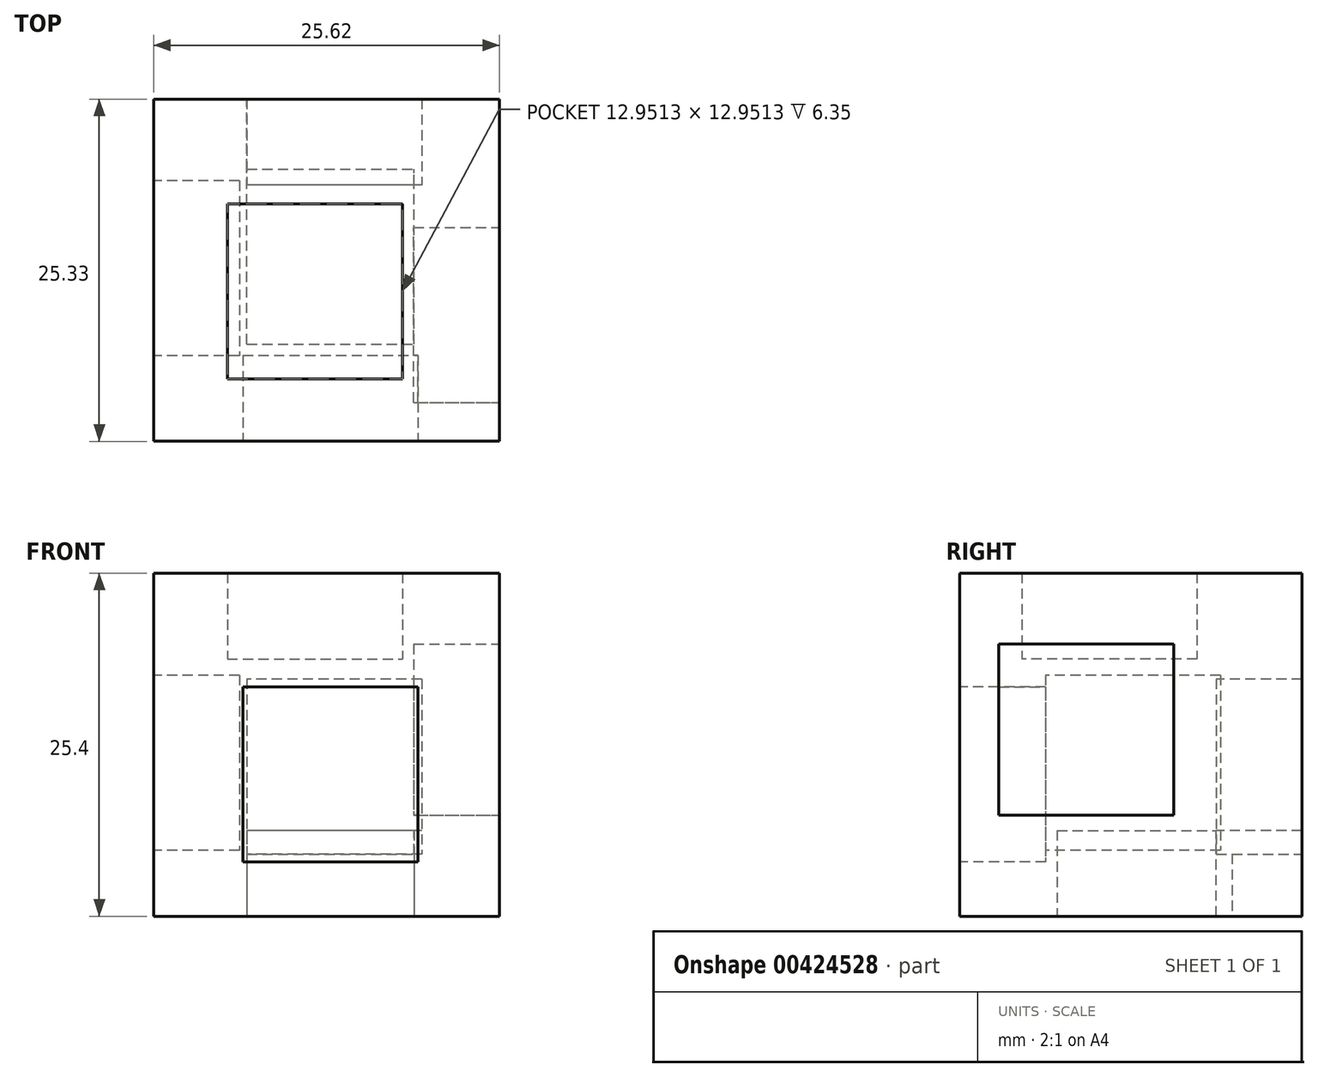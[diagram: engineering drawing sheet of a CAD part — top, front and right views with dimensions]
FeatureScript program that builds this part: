
annotation { "Feature Type Name" : "Feature", "Feature Type Description" : "" }
export const myFeature = defineFeature(function(context is Context, id is Id, definition is map)
    precondition{}
    {
        {
            var Q0;
            Q0=qCreatedBy(makeId("Top.planeOp"),FACE);
            var sketch = newSketch(context, id + "F0", { "sketchPlane" : qUnion([Q0])});
            skLineSegment(sketch, "E0.bottom", {"start": v(-29.36, 32.52) * mm, "end": v(-3.74, 32.52) * mm});
            skLineSegment(sketch, "E0.top", {"start": v(-29.36, 7.2) * mm, "end": v(-3.74, 7.2) * mm});
            skLineSegment(sketch, "E0.left", {"start": v(-29.36, 32.52) * mm, "end": v(-29.36, 7.2) * mm});
            skLineSegment(sketch, "E0.right", {"start": v(-3.74, 32.52) * mm, "end": v(-3.74, 7.2) * mm});
            skSolve(sketch);
        }
        {
            var Q0;
            Q0=makeQuery(id+"F0.imprint","IMPRINT",FACE,{"disambiguationData":[TD([[makeQuery(id+"F0.imprint","IMPRINT",EDGE,{"derivedFrom":sQuery(id+"F0.wireOp",EDGE,"E0.bottom")}),-1.0]])]});
            extrude(context, id + "F1", {"entities" : qUnion([Q0]), "depth" : 25.4 * mm});
        }
        {
            var Q0;
            Q0=makeQuery(id+"F1.opExtrude","SWEPT_FACE",FACE,{"disambiguationData":[OSD([sQuery(id+"F0.wireOp",EDGE,"E0.right")])]});
            var sketch = newSketch(context, id + "F2", { "sketchPlane" : qUnion([Q0])});
            skLineSegment(sketch, "E1.bottom", {"start": v(10.07, 20.15) * mm, "end": v(23.02, 20.15) * mm});
            skLineSegment(sketch, "E1.top", {"start": v(10.07, 7.48) * mm, "end": v(23.02, 7.48) * mm});
            skLineSegment(sketch, "E1.left", {"start": v(10.07, 20.15) * mm, "end": v(10.07, 7.48) * mm});
            skLineSegment(sketch, "E1.right", {"start": v(23.02, 20.15) * mm, "end": v(23.02, 7.48) * mm});
            skSolve(sketch);
        }
        {
            var Q0;
            Q0=makeQuery(id+"F2.imprint","IMPRINT",FACE,{"disambiguationData":[TD([[makeQuery(id+"F2.imprint","IMPRINT",EDGE,{"derivedFrom":sQuery(id+"F2.wireOp",EDGE,"E1.bottom")}),-1.0]])]});
            extrude(context, id + "F3", {"entities" : qUnion([Q0]), "operationType" : NewBodyOperationType.REMOVE, "oppositeDirection" : true, "depth" : 6.35 * mm});
        }
        {
            var Q0;
            Q0=makeQuery(id+"F1.opExtrude","SWEPT_FACE",FACE,{"disambiguationData":[OSD([sQuery(id+"F0.wireOp",EDGE,"E0.left")])]});
            var sketch = newSketch(context, id + "F4", { "sketchPlane" : qUnion([Q0])});
            skLineSegment(sketch, "E2.bottom", {"start": v(-26.48, 17.84) * mm, "end": v(-13.53, 17.84) * mm});
            skLineSegment(sketch, "E2.top", {"start": v(-26.48, 4.9) * mm, "end": v(-13.53, 4.9) * mm});
            skLineSegment(sketch, "E2.left", {"start": v(-26.48, 17.84) * mm, "end": v(-26.48, 4.9) * mm});
            skLineSegment(sketch, "E2.right", {"start": v(-13.53, 17.84) * mm, "end": v(-13.53, 4.9) * mm});
            skSolve(sketch);
        }
        {
            var Q0;
            Q0 = qSketchRegion(id + "F4", true);
            extrude(context, id + "F5", {"entities" : qUnion([Q0]), "operationType" : NewBodyOperationType.REMOVE, "oppositeDirection" : true, "depth" : 6.35 * mm});
        }
        {
            var Q0;
            Q0=makeQuery(id+"F1.opExtrude","CAP_FACE",FACE,{"disambiguationData":[OSD([sQuery(id+"F0.wireOp",EDGE,"E0.bottom"),sQuery(id+"F0.wireOp",EDGE,"E0.top"),sQuery(id+"F0.wireOp",EDGE,"E0.left"),sQuery(id+"F0.wireOp",EDGE,"E0.right")])],"isStart":false});
            var sketch = newSketch(context, id + "F6", { "sketchPlane" : qUnion([Q0])});
            skLineSegment(sketch, "E3.bottom", {"start": v(-23.89, 24.75) * mm, "end": v(-10.94, 24.75) * mm});
            skLineSegment(sketch, "E3.top", {"start": v(-23.89, 11.8) * mm, "end": v(-10.94, 11.8) * mm});
            skLineSegment(sketch, "E3.left", {"start": v(-23.89, 24.75) * mm, "end": v(-23.89, 11.8) * mm});
            skLineSegment(sketch, "E3.right", {"start": v(-10.94, 24.75) * mm, "end": v(-10.94, 11.8) * mm});
            skSolve(sketch);
        }
        {
            var Q0;
            Q0 = qSketchRegion(id + "F6", true);
            extrude(context, id + "F7", {"entities" : qUnion([Q0]), "operationType" : NewBodyOperationType.REMOVE, "oppositeDirection" : true, "depth" : 6.35 * mm});
        }
        {
            var Q0;
            Q0=makeQuery(id+"F1.opExtrude","SWEPT_FACE",FACE,{"disambiguationData":[OSD([sQuery(id+"F0.wireOp",EDGE,"E0.bottom")])]});
            var sketch = newSketch(context, id + "F8", { "sketchPlane" : qUnion([Q0])});
            skLineSegment(sketch, "E4.bottom", {"start": v(9.5, 17.56) * mm, "end": v(22.45, 17.56) * mm});
            skLineSegment(sketch, "E4.top", {"start": v(9.5, 4.6) * mm, "end": v(22.45, 4.6) * mm});
            skLineSegment(sketch, "E4.left", {"start": v(9.5, 17.56) * mm, "end": v(9.5, 4.6) * mm});
            skLineSegment(sketch, "E4.right", {"start": v(22.45, 17.56) * mm, "end": v(22.45, 4.6) * mm});
            skSolve(sketch);
        }
        {
            var Q0;
            Q0 = qSketchRegion(id + "F8", true);
            extrude(context, id + "F9", {"entities" : qUnion([Q0]), "operationType" : NewBodyOperationType.REMOVE, "oppositeDirection" : true, "depth" : 6.35 * mm});
        }
        {
            var Q0;
            Q0=makeQuery(id+"F1.opExtrude","SWEPT_FACE",FACE,{"disambiguationData":[OSD([sQuery(id+"F0.wireOp",EDGE,"E0.top")])]});
            var sketch = newSketch(context, id + "F10", { "sketchPlane" : qUnion([Q0])});
            skLineSegment(sketch, "E5.bottom", {"start": v(-22.74, 16.98) * mm, "end": v(-9.79, 16.98) * mm});
            skLineSegment(sketch, "E5.top", {"start": v(-22.74, 4.03) * mm, "end": v(-9.79, 4.03) * mm});
            skLineSegment(sketch, "E5.left", {"start": v(-22.74, 16.98) * mm, "end": v(-22.74, 4.03) * mm});
            skLineSegment(sketch, "E5.right", {"start": v(-9.79, 16.98) * mm, "end": v(-9.79, 4.03) * mm});
            skSolve(sketch);
        }
        {
            var Q0;
            Q0=makeQuery(id+"F10.imprint","IMPRINT",FACE,{"disambiguationData":[TD([[makeQuery(id+"F10.imprint","IMPRINT",EDGE,{"derivedFrom":sQuery(id+"F10.wireOp",EDGE,"E5.bottom")}),-1.0]])]});
            extrude(context, id + "F11", {"entities" : qUnion([Q0]), "operationType" : NewBodyOperationType.REMOVE, "oppositeDirection" : true, "depth" : 6.35 * mm});
        }
        {
            var Q0;
            Q0=makeQuery(id+"F1.opExtrude","CAP_FACE",FACE,{"disambiguationData":[OSD([sQuery(id+"F0.wireOp",EDGE,"E0.bottom"),sQuery(id+"F0.wireOp",EDGE,"E0.top"),sQuery(id+"F0.wireOp",EDGE,"E0.left"),sQuery(id+"F0.wireOp",EDGE,"E0.right")])],"isStart":true});
            var sketch = newSketch(context, id + "F12", { "sketchPlane" : qUnion([Q0])});
            skLineSegment(sketch, "E6.bottom", {"start": v(-22.45, -14.4) * mm, "end": v(-10.07, -14.4) * mm});
            skLineSegment(sketch, "E6.top", {"start": v(-22.45, -27.34) * mm, "end": v(-10.07, -27.34) * mm});
            skLineSegment(sketch, "E6.left", {"start": v(-22.45, -14.4) * mm, "end": v(-22.45, -27.34) * mm});
            skLineSegment(sketch, "E6.right", {"start": v(-10.07, -14.4) * mm, "end": v(-10.07, -27.34) * mm});
            skSolve(sketch);
        }
        {
            var Q0;
            Q0 = qSketchRegion(id + "F12", true);
            extrude(context, id + "F13", {"entities" : qUnion([Q0]), "operationType" : NewBodyOperationType.REMOVE, "oppositeDirection" : true, "depth" : 6.35 * mm});
        }
        {
            var Q0;
            Q0=makeQuery(id+"F7.boolean.opBoolean","COPY",FACE,{"derivedFrom":makeQuery(id+"F7.opExtrude","CAP_FACE",FACE,{"disambiguationData":[OSD([sQuery(id+"F6.wireOp",EDGE,"E3.bottom"),sQuery(id+"F6.wireOp",EDGE,"E3.top"),sQuery(id+"F6.wireOp",EDGE,"E3.left"),sQuery(id+"F6.wireOp",EDGE,"E3.right")])],"isStart":false})});
            var sketch = newSketch(context, id + "F14", { "sketchPlane" : qUnion([Q0])});
            skLineSegment(sketch, "E7.bottom", {"start": v(-23.89, 24.75) * mm, "end": v(-10.94, 24.75) * mm});
            skLineSegment(sketch, "E7.top", {"start": v(-23.89, 11.8) * mm, "end": v(-10.94, 11.8) * mm});
            skLineSegment(sketch, "E7.left", {"start": v(-23.89, 24.75) * mm, "end": v(-23.89, 11.8) * mm});
            skLineSegment(sketch, "E7.right", {"start": v(-10.94, 24.75) * mm, "end": v(-10.94, 11.8) * mm});
            skSolve(sketch);
        }
        {
            var Q0;
            Q0 = qSketchRegion(id + "F14", true);
            extrude(context, id + "F15", {"entities" : qUnion([Q0]), "depth" : 6.35 * mm});
        }
        {
            var Q0;
            Q0=makeQuery(id+"F9.boolean.opBoolean","COPY",FACE,{"derivedFrom":makeQuery(id+"F9.opExtrude","CAP_FACE",FACE,{"disambiguationData":[OSD([sQuery(id+"F8.wireOp",EDGE,"E4.bottom"),sQuery(id+"F8.wireOp",EDGE,"E4.top"),sQuery(id+"F8.wireOp",EDGE,"E4.left"),sQuery(id+"F8.wireOp",EDGE,"E4.right")])],"isStart":false})});
            var sketch = newSketch(context, id + "F16", { "sketchPlane" : qUnion([Q0])});
            skLineSegment(sketch, "E8.bottom", {"start": v(9.5, 17.56) * mm, "end": v(22.45, 17.56) * mm});
            skLineSegment(sketch, "E8.top", {"start": v(9.5, 6.35) * mm, "end": v(22.45, 6.35) * mm});
            skLineSegment(sketch, "E8.left", {"start": v(9.5, 17.56) * mm, "end": v(9.5, 6.35) * mm});
            skLineSegment(sketch, "E8.right", {"start": v(22.45, 17.56) * mm, "end": v(22.45, 6.35) * mm});
            skSolve(sketch);
        }
        {
            var Q0;
            Q0 = qSketchRegion(id + "F16", true);
            extrude(context, id + "F17", {"entities" : qUnion([Q0]), "depth" : 6.35 * mm});
        }
        {
            var Q0;
            Q0=makeQuery(id+"F5.boolean.opBoolean","COPY",FACE,{"derivedFrom":makeQuery(id+"F5.opExtrude","CAP_FACE",FACE,{"disambiguationData":[OSD([sQuery(id+"F4.wireOp",EDGE,"E2.bottom"),sQuery(id+"F4.wireOp",EDGE,"E2.top"),sQuery(id+"F4.wireOp",EDGE,"E2.left"),sQuery(id+"F4.wireOp",EDGE,"E2.right")])],"isStart":false})});
            var sketch = newSketch(context, id + "F18", { "sketchPlane" : qUnion([Q0])});
            skLineSegment(sketch, "E9.bottom", {"start": v(-26.48, 17.84) * mm, "end": v(-13.53, 17.84) * mm});
            skLineSegment(sketch, "E9.top", {"start": v(-26.48, 4.9) * mm, "end": v(-13.53, 4.9) * mm});
            skLineSegment(sketch, "E9.left", {"start": v(-26.48, 17.84) * mm, "end": v(-26.48, 4.9) * mm});
            skLineSegment(sketch, "E9.right", {"start": v(-13.53, 17.84) * mm, "end": v(-13.53, 4.9) * mm});
            skSolve(sketch);
        }
        {
            var Q0;
            Q0 = qSketchRegion(id + "F18", true);
            extrude(context, id + "F19", {"entities" : qUnion([Q0]), "depth" : 6.35 * mm});
        }
        {
            var Q0;
            Q0=makeQuery(id+"F11.boolean.opBoolean","COPY",FACE,{"derivedFrom":makeQuery(id+"F11.opExtrude","CAP_FACE",FACE,{"disambiguationData":[OSD([sQuery(id+"F10.wireOp",EDGE,"E5.bottom"),sQuery(id+"F10.wireOp",EDGE,"E5.top"),sQuery(id+"F10.wireOp",EDGE,"E5.left"),sQuery(id+"F10.wireOp",EDGE,"E5.right")])],"isStart":false})});
            var sketch = newSketch(context, id + "F20", { "sketchPlane" : qUnion([Q0])});
            skLineSegment(sketch, "E10.bottom", {"start": v(-22.74, 16.98) * mm, "end": v(-9.79, 16.98) * mm});
            skLineSegment(sketch, "E10.top", {"start": v(-22.74, 4.03) * mm, "end": v(-9.79, 4.03) * mm});
            skLineSegment(sketch, "E10.left", {"start": v(-22.74, 16.98) * mm, "end": v(-22.74, 4.03) * mm});
            skLineSegment(sketch, "E10.right", {"start": v(-9.79, 16.98) * mm, "end": v(-9.79, 4.03) * mm});
            skSolve(sketch);
        }
        {
            var Q0;
            Q0 = qSketchRegion(id + "F20", true);
            extrude(context, id + "F21", {"entities" : qUnion([Q0]), "depth" : 6.35 * mm});
        }
        {
            var Q0;
            Q0=makeQuery(id+"F13.boolean.opBoolean","COPY",FACE,{"derivedFrom":makeQuery(id+"F13.opExtrude","CAP_FACE",FACE,{"disambiguationData":[OSD([sQuery(id+"F12.wireOp",EDGE,"E6.bottom"),sQuery(id+"F12.wireOp",EDGE,"E6.top"),sQuery(id+"F12.wireOp",EDGE,"E6.left"),sQuery(id+"F12.wireOp",EDGE,"E6.right")])],"isStart":false})});
            var sketch = newSketch(context, id + "F22", { "sketchPlane" : qUnion([Q0])});
            skLineSegment(sketch, "E11.bottom", {"start": v(-22.45, -14.4) * mm, "end": v(-10.07, -14.4) * mm});
            skLineSegment(sketch, "E11.top", {"start": v(-22.45, -26.17) * mm, "end": v(-10.07, -26.17) * mm});
            skLineSegment(sketch, "E11.left", {"start": v(-22.45, -14.4) * mm, "end": v(-22.45, -26.17) * mm});
            skLineSegment(sketch, "E11.right", {"start": v(-10.07, -14.4) * mm, "end": v(-10.07, -26.17) * mm});
            skSolve(sketch);
        }
        {
            var Q0;
            Q0 = qSketchRegion(id + "F22", true);
            extrude(context, id + "F23", {"entities" : qUnion([Q0]), "depth" : 6.35 * mm});
        }
        {
            var Q0;
            Q0=makeQuery(id+"F3.boolean.opBoolean","COPY",FACE,{"derivedFrom":makeQuery(id+"F3.opExtrude","CAP_FACE",FACE,{"disambiguationData":[OSD([sQuery(id+"F2.wireOp",EDGE,"E1.bottom"),sQuery(id+"F2.wireOp",EDGE,"E1.top"),sQuery(id+"F2.wireOp",EDGE,"E1.left"),sQuery(id+"F2.wireOp",EDGE,"E1.right")])],"isStart":false})});
            var sketch = newSketch(context, id + "F24", { "sketchPlane" : qUnion([Q0])});
            skLineSegment(sketch, "E12.bottom", {"start": v(10.07, 20.15) * mm, "end": v(23.02, 20.15) * mm});
            skLineSegment(sketch, "E12.top", {"start": v(10.07, 7.48) * mm, "end": v(23.02, 7.48) * mm});
            skLineSegment(sketch, "E12.left", {"start": v(10.07, 20.15) * mm, "end": v(10.07, 7.48) * mm});
            skLineSegment(sketch, "E12.right", {"start": v(23.02, 20.15) * mm, "end": v(23.02, 7.48) * mm});
            skSolve(sketch);
        }
        {
            var Q0;
            Q0 = qSketchRegion(id + "F24", true);
            extrude(context, id + "F25", {"entities" : qUnion([Q0]), "depth" : 6.35 * mm});
        }
    });
